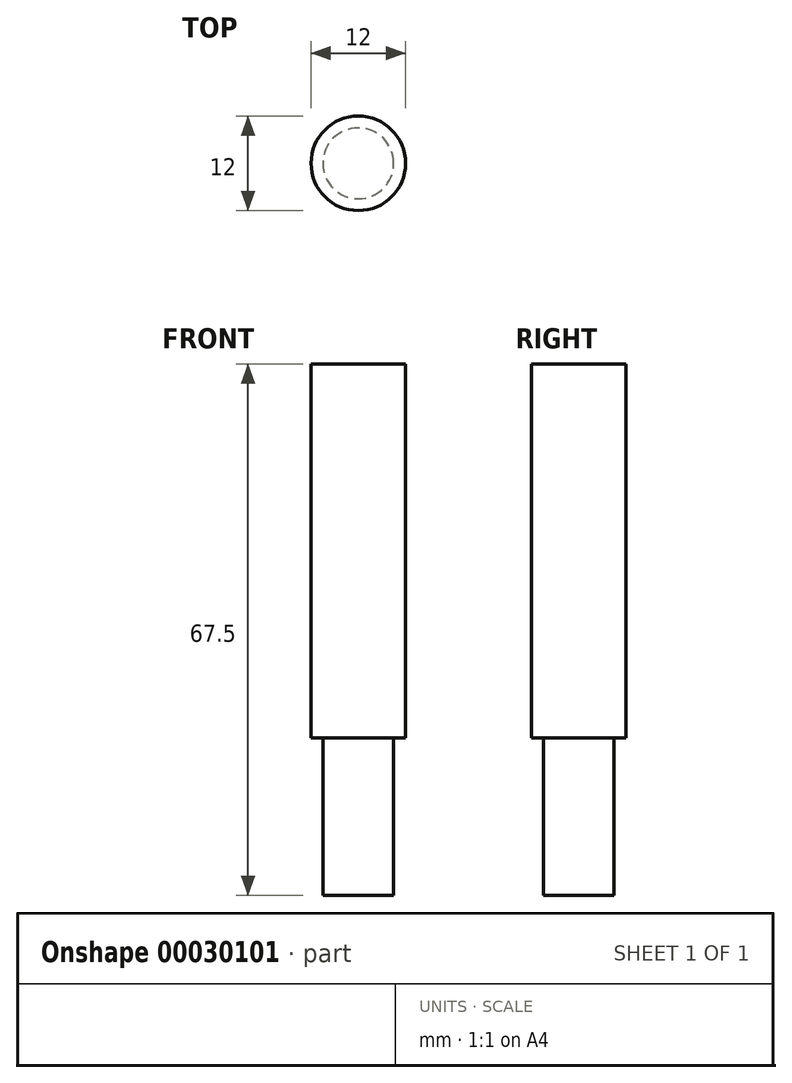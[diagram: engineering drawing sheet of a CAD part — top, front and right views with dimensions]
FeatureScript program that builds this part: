
annotation { "Feature Type Name" : "Feature", "Feature Type Description" : "" }
export const myFeature = defineFeature(function(context is Context, id is Id, definition is map)
    precondition{}
    {
        {
            var Q0;
            Q0=qCreatedBy(makeId("Right.planeOp"),FACE);
            var sketch = newSketch(context, id + "F0", { "sketchPlane" : qUnion([Q0])});
            skLineSegment(sketch, "E0", {"start": v(0, 0) * mm, "end": v(4.5, 0) * mm});
            skLineSegment(sketch, "E1", {"start": v(4.5, 0) * mm, "end": v(4.5, 20) * mm});
            skLineSegment(sketch, "E2", {"start": v(4.5, 20) * mm, "end": v(6, 20) * mm});
            skLineSegment(sketch, "E3", {"start": v(6, 20) * mm, "end": v(6, 67.5) * mm});
            skLineSegment(sketch, "E4", {"start": v(6, 67.5) * mm, "end": v(0, 67.5) * mm});
            skLineSegment(sketch, "E5", {"start": v(0, 67.5) * mm, "end": v(0, 0) * mm, "construction": true});
            skLineSegment(sketch, "E6", {"start": v(0, 67.5) * mm, "end": v(0, 0) * mm});
            skSolve(sketch);
        }
        {
            var Q0;
            Q0=makeQuery(id+"F0.imprint","IMPRINT",FACE,{"disambiguationData":[TD([[makeQuery(id+"F0.imprint","IMPRINT",EDGE,{"derivedFrom":sQuery(id+"F0.wireOp",EDGE,"E0")}),1.0]])]});
            var Q1;
            Q1=sQuery(id+"F0.wireOp",EDGE,"E5");
            revolve(context, id + "F1", {"entities" : qUnion([Q0]), "axis" : qUnion([Q1]), "revolveType" : RevolveType.FULL});
        }
    });
